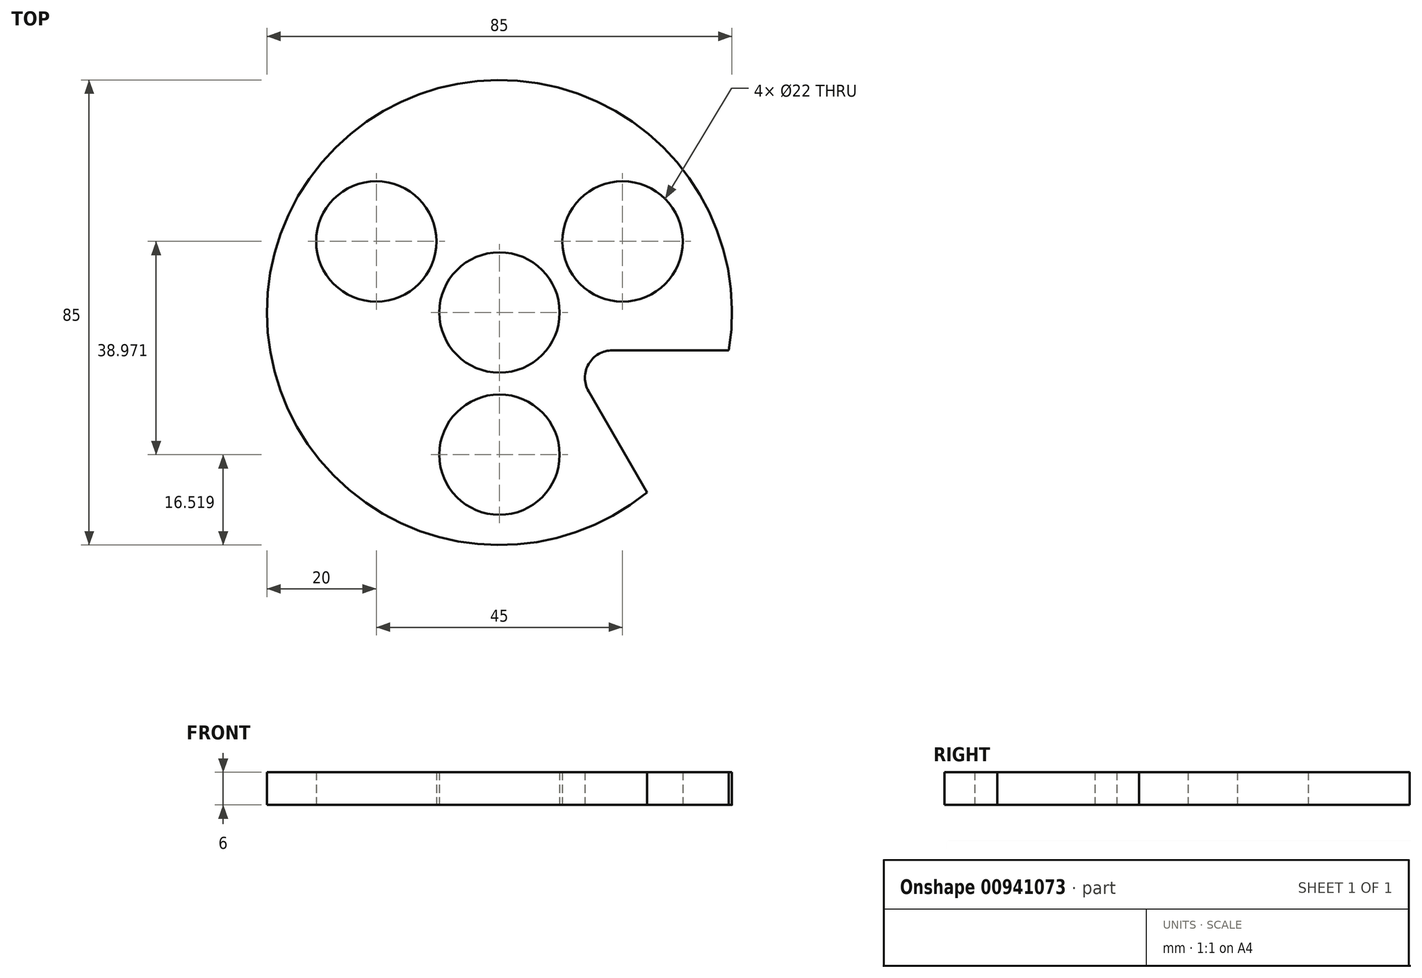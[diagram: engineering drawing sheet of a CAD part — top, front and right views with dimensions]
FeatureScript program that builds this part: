
annotation { "Feature Type Name" : "Feature", "Feature Type Description" : "" }
export const myFeature = defineFeature(function(context is Context, id is Id, definition is map)
    precondition{}
    {
        {
            var Q0;
            Q0=qCreatedBy(makeId("Top.planeOp"),FACE);
            var sketch = newSketch(context, id + "F0", { "sketchPlane" : qUnion([Q0])});
            skCircle(sketch, "E0", {"center": v(0, 0) * mm, "radius": 42.5 * mm});
            skCircle(sketch, "E1", {"center": v(0, 0) * mm, "radius": 11 * mm});
            skCircle(sketch, "E2.cCircle", {"center": v(0, 0) * mm, "radius": 13 * mm, "construction": true});
            skLineSegment(sketch, "E2.0", {"start": v(22.5, 13) * mm, "end": v(0, -25.98) * mm, "construction": true});
            skLineSegment(sketch, "E2.1", {"start": v(0, -25.98) * mm, "end": v(-22.5, 13) * mm, "construction": true});
            skLineSegment(sketch, "E2.2", {"start": v(-22.5, 13) * mm, "end": v(22.5, 13) * mm, "construction": true});
            skPoint(sketch, "E2.0.midPoint", {"position": v(11.25, -6.5) * mm});
            skCircle(sketch, "E3", {"center": v(0, -25.98) * mm, "radius": 11 * mm});
            skCircle(sketch, "E4", {"center": v(-22.5, 13) * mm, "radius": 11 * mm});
            skCircle(sketch, "E5", {"center": v(22.5, 13) * mm, "radius": 11 * mm});
            skSolve(sketch);
        }
        {
            var Q0;
            Q0=makeQuery(id+"F0.imprint","IMPRINT",FACE,{"disambiguationData":[TD([[makeQuery(id+"F0.imprint","IMPRINT",EDGE,{"derivedFrom":sQuery(id+"F0.wireOp",EDGE,"E0")}),1.0]])]});
            extrude(context, id + "F1", {"entities" : qUnion([Q0]), "depth" : 6 * mm, "offsetDistance" : 25 * mm});
        }
        {
            var Q0;
            Q0=makeQuery(id+"F1.opExtrude","CAP_FACE",FACE,{"disambiguationData":[OSD([sQuery(id+"F0.wireOp",EDGE,"E0"),sQuery(id+"F0.wireOp",EDGE,"E1"),sQuery(id+"F0.wireOp",EDGE,"E3"),sQuery(id+"F0.wireOp",EDGE,"E4"),sQuery(id+"F0.wireOp",EDGE,"E5")])],"isStart":false});
            var sketch = newSketch(context, id + "F2", { "sketchPlane" : qUnion([Q0])});
            skCircle(sketch, "E6.0", {"center": v(0, 0) * mm, "radius": 42.5 * mm});
            skLineSegment(sketch, "E7", {"start": v(0, 0) * mm, "end": v(0, -53.63) * mm, "construction": true});
            skLineSegment(sketch, "E8", {"start": v(0, 0) * mm, "end": v(57.63, -33.28) * mm, "construction": true});
            skPoint(sketch, "E9.cCircle.perimeterSnap0", {"position": v(28.82, -16.64) * mm});
            skPoint(sketch, "E9.0.midPoint", {"position": v(28.82, -12.29) * mm});
            skPoint(sketch, "E9.0.midPoint.positionSnap0", {"position": v(28.82, -16.64) * mm});
            skCircle(sketch, "E10.cCircle", {"center": v(28.82, -16.64) * mm, "radius": 9.72 * mm, "construction": true});
            skLineSegment(sketch, "E10.0", {"start": v(45.66, -6.91) * mm, "end": v(28.82, -36.09) * mm});
            skLineSegment(sketch, "E10.1", {"start": v(28.82, -36.09) * mm, "end": v(11.97, -6.91) * mm});
            skLineSegment(sketch, "E10.2", {"start": v(11.97, -6.91) * mm, "end": v(45.66, -6.91) * mm});
            skPoint(sketch, "E10.0.midPoint", {"position": v(37.24, -21.5) * mm});
            skSolve(sketch);
        }
        {
            var Q0;
            {var subQ0=sQuery(id+"F2.wireOp",EDGE,"E10.1");var subQ1=sQuery(id+"F2.wireOp",EDGE,"E6.0");var subQ2=makeQuery(id+"F2.imprint","INTERSECT",VERTEX,{"derivedFrom":[subQ1,subQ0]});Q0=makeQuery(id+"F2.imprint","IMPRINT",FACE,{"disambiguationData":[TD([[makeQuery(id+"F2.imprint","IMPRINT",EDGE,{"disambiguationData":[TD([[subQ2,-1.0]])],"derivedFrom":subQ1}),1.0]])]});}
            extrude(context, id + "F3", {"entities" : qUnion([Q0]), "operationType" : NewBodyOperationType.REMOVE, "oppositeDirection" : true, "depth" : 25 * mm, "offsetDistance" : 25 * mm});
        }
        {
            var Q0;
            Q0=makeQuery(id+"F3.boolean.opBoolean","COPY",EDGE,{"derivedFrom":makeQuery(id+"F3.opExtrude","SWEPT_EDGE",EDGE,{"disambiguationData":[OSD([sQuery(id+"F2.wireOp",EDGE,"E10.1"),sQuery(id+"F2.wireOp",EDGE,"E10.2")])]})});
            fillet(context, id + "F4", {"entities" : qUnion([Q0]), "radius" : 5 * mm, "tangentPropagation" : true, "allowEdgeOverflow" : false});
        }
    });
